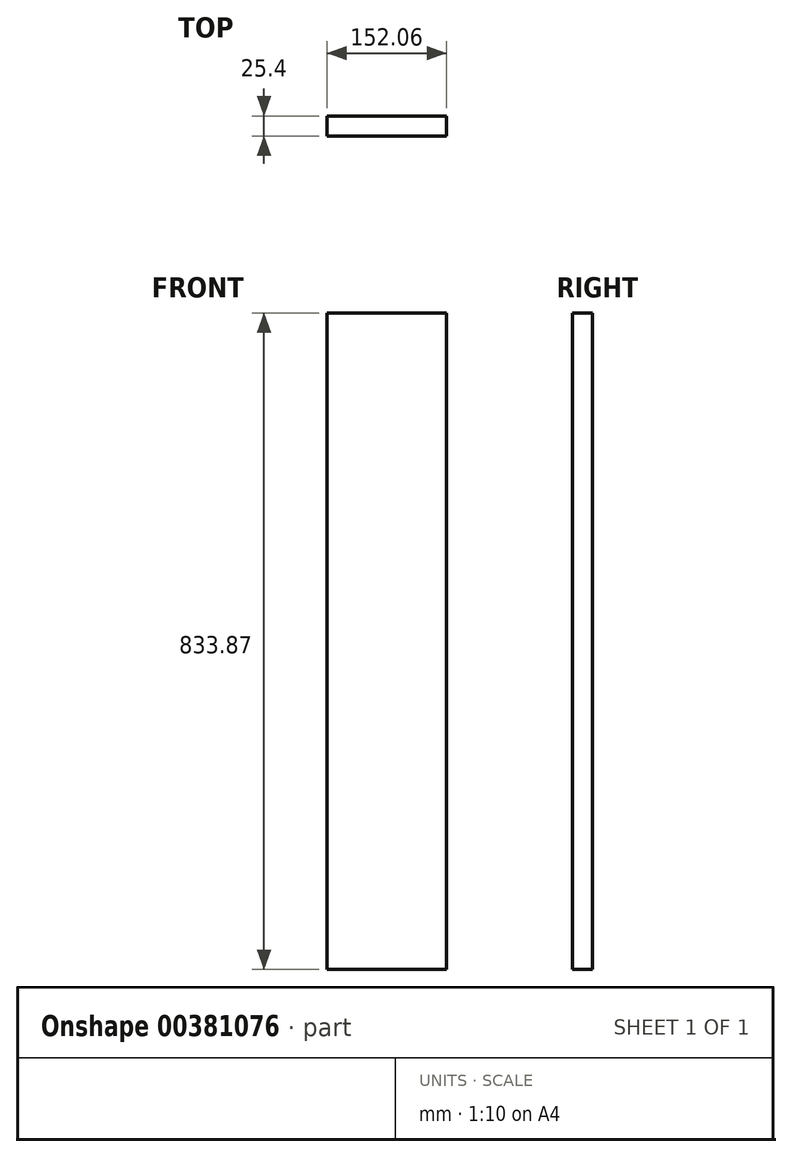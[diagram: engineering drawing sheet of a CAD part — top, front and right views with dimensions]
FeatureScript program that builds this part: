
annotation { "Feature Type Name" : "Feature", "Feature Type Description" : "" }
export const myFeature = defineFeature(function(context is Context, id is Id, definition is map)
    precondition{}
    {
        {
            var Q0;
            Q0=qCreatedBy(makeId("Front.planeOp"),FACE);
            var sketch = newSketch(context, id + "F0", { "sketchPlane" : qUnion([Q0])});
            skLineSegment(sketch, "E0.bottom", {"start": v(-56.55, 138.72) * mm, "end": v(95.51, 138.72) * mm});
            skLineSegment(sketch, "E0.top", {"start": v(-56.55, -695.15) * mm, "end": v(95.51, -695.15) * mm});
            skLineSegment(sketch, "E0.left", {"start": v(-56.55, 138.72) * mm, "end": v(-56.55, -695.15) * mm});
            skLineSegment(sketch, "E0.right", {"start": v(95.51, 138.72) * mm, "end": v(95.51, -695.15) * mm});
            skSolve(sketch);
        }
        {
            var Q0;
            Q0 = qSketchRegion(id + "F0", true);
            extrude(context, id + "F1", {"entities" : qUnion([Q0]), "depth" : 25.4 * mm});
        }
    });
